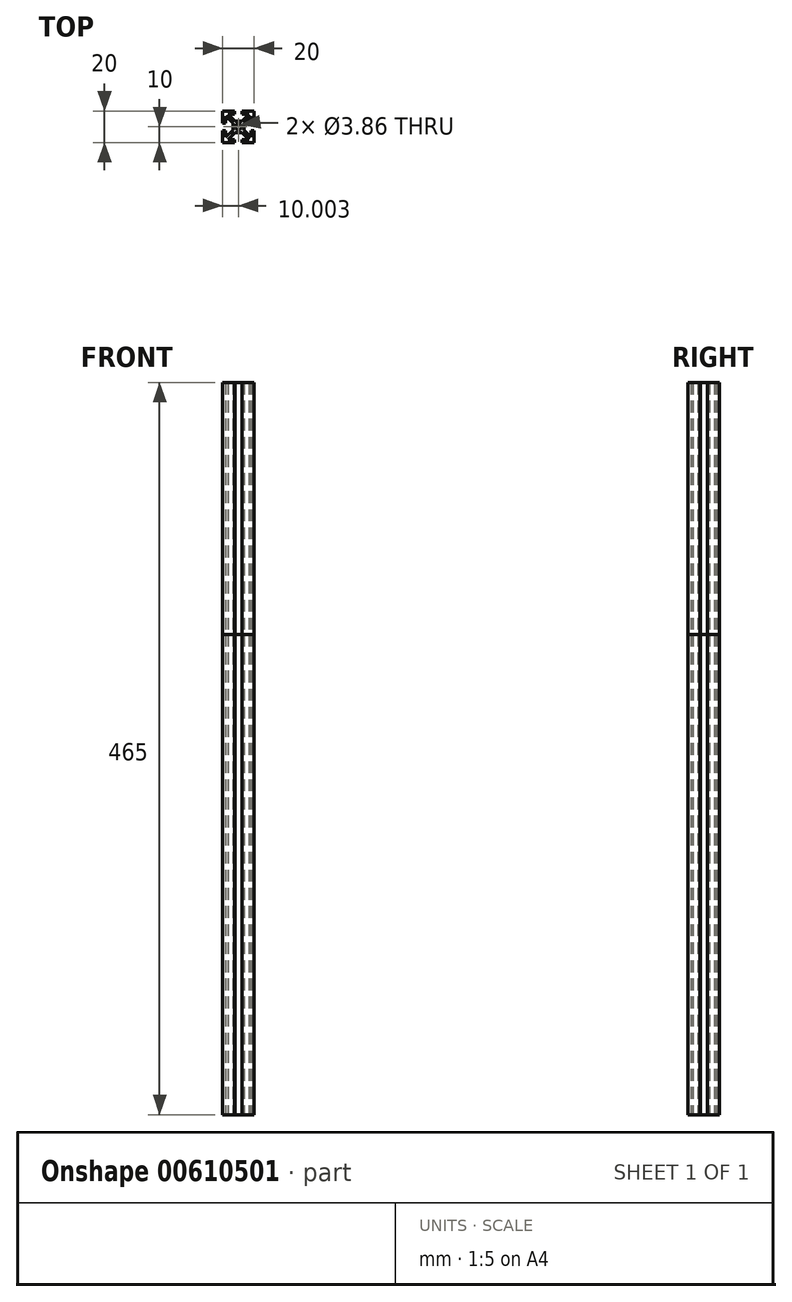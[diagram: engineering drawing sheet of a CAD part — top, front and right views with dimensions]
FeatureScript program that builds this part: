
annotation { "Feature Type Name" : "Feature", "Feature Type Description" : "" }
export const myFeature = defineFeature(function(context is Context, id is Id, definition is map)
    precondition{}
    {
        {
            var Q0;
            Q0=qCreatedBy(makeId("Top.planeOp"),FACE);
            var sketch = newSketch(context, id + "F0", { "sketchPlane" : qUnion([Q0])});
            skCircle(sketch, "E0.0", {"center": v(0, 0) * mm, "radius": 1.93 * mm});
            skLineSegment(sketch, "E0.1", {"start": v(-2.2, 3.6) * mm, "end": v(2.2, 3.6) * mm});
            skLineSegment(sketch, "E0.2", {"start": v(-6.72, 8.13) * mm, "end": v(-2.2, 3.6) * mm});
            skLineSegment(sketch, "E0.3", {"start": v(-3.6, 2.24) * mm, "end": v(-8.1, 6.74) * mm});
            skLineSegment(sketch, "E0.4", {"start": v(-8.1, 6.74) * mm, "end": v(-8.1, 2.38) * mm});
            skLineSegment(sketch, "E0.5", {"start": v(-8.1, 2.38) * mm, "end": v(-10, 2.38) * mm});
            skLineSegment(sketch, "E0.6", {"start": v(-10, 2.38) * mm, "end": v(-10, 10) * mm});
            skLineSegment(sketch, "E0.7", {"start": v(-10, 10) * mm, "end": v(-2.38, 10) * mm});
            skLineSegment(sketch, "E0.8", {"start": v(-2.38, 10) * mm, "end": v(-2.38, 8.13) * mm});
            skLineSegment(sketch, "E0.9", {"start": v(-2.38, 8.13) * mm, "end": v(-6.72, 8.13) * mm});
            skLineSegment(sketch, "E0.10", {"start": v(2.2, 3.6) * mm, "end": v(6.73, 8.13) * mm});
            skLineSegment(sketch, "E0.11", {"start": v(8.1, 6.74) * mm, "end": v(3.6, 2.24) * mm});
            skLineSegment(sketch, "E0.12", {"start": v(2.38, 8.13) * mm, "end": v(6.73, 8.13) * mm});
            skLineSegment(sketch, "E0.13", {"start": v(2.38, 8.13) * mm, "end": v(2.38, 10) * mm});
            skLineSegment(sketch, "E0.14", {"start": v(2.38, 10) * mm, "end": v(10, 10) * mm});
            skLineSegment(sketch, "E0.15", {"start": v(10, 10) * mm, "end": v(10, 2.38) * mm});
            skLineSegment(sketch, "E0.16", {"start": v(8.1, 2.38) * mm, "end": v(8.1, 6.74) * mm});
            skLineSegment(sketch, "E0.17", {"start": v(10, 2.38) * mm, "end": v(8.1, 2.38) * mm});
            skLineSegment(sketch, "E0.18", {"start": v(3.6, 2.24) * mm, "end": v(3.6, -2.24) * mm});
            skLineSegment(sketch, "E0.19", {"start": v(3.6, -2.24) * mm, "end": v(8.1, -6.74) * mm});
            skLineSegment(sketch, "E0.20", {"start": v(8.1, -6.74) * mm, "end": v(8.1, -2.38) * mm});
            skLineSegment(sketch, "E0.21", {"start": v(8.1, -2.38) * mm, "end": v(10, -2.38) * mm});
            skLineSegment(sketch, "E0.22", {"start": v(10, -2.38) * mm, "end": v(10, -10) * mm});
            skLineSegment(sketch, "E0.23", {"start": v(10, -10) * mm, "end": v(2.38, -10) * mm});
            skLineSegment(sketch, "E0.24", {"start": v(2.38, -10) * mm, "end": v(2.38, -8.13) * mm});
            skLineSegment(sketch, "E0.25", {"start": v(2.38, -8.13) * mm, "end": v(6.72, -8.13) * mm});
            skLineSegment(sketch, "E0.26", {"start": v(6.72, -8.13) * mm, "end": v(2.2, -3.6) * mm});
            skLineSegment(sketch, "E0.27", {"start": v(2.2, -3.6) * mm, "end": v(-2.2, -3.6) * mm});
            skLineSegment(sketch, "E0.28", {"start": v(-2.2, -3.6) * mm, "end": v(-6.73, -8.13) * mm});
            skLineSegment(sketch, "E0.29", {"start": v(-8.1, -6.74) * mm, "end": v(-3.6, -2.24) * mm});
            skLineSegment(sketch, "E0.30", {"start": v(-3.6, -2.24) * mm, "end": v(-3.6, 2.24) * mm});
            skLineSegment(sketch, "E0.31", {"start": v(-8.1, -2.38) * mm, "end": v(-8.1, -6.74) * mm});
            skLineSegment(sketch, "E0.32", {"start": v(-10, -2.38) * mm, "end": v(-8.1, -2.38) * mm});
            skLineSegment(sketch, "E0.33", {"start": v(-10, -10) * mm, "end": v(-10, -2.38) * mm});
            skLineSegment(sketch, "E0.34", {"start": v(-2.38, -10) * mm, "end": v(-10, -10) * mm});
            skLineSegment(sketch, "E0.35", {"start": v(-6.73, -8.13) * mm, "end": v(-2.38, -8.13) * mm});
            skLineSegment(sketch, "E0.36", {"start": v(-2.38, -8.13) * mm, "end": v(-2.38, -10) * mm});
            skSolve(sketch);
        }
        {
            var Q0;
            Q0=makeQuery(id+"F0.imprint","IMPRINT",FACE,{"disambiguationData":[TD([[makeQuery(id+"F0.imprint","IMPRINT",EDGE,{"derivedFrom":sQuery(id+"F0.wireOp",EDGE,"E0.0")}),-1.0]])]});
            extrude(context, id + "F1", {"entities" : qUnion([Q0]), "depth" : 305 * mm, "offsetDistance" : 25.4 * mm});
        }
        {
            var Q0;
            Q0=makeQuery(id+"F1.opExtrude","CAP_FACE",FACE,{"disambiguationData":[OSD([sQuery(id+"F0.wireOp",EDGE,"E0.0"),sQuery(id+"F0.wireOp",EDGE,"E0.1"),sQuery(id+"F0.wireOp",EDGE,"E0.2"),sQuery(id+"F0.wireOp",EDGE,"E0.3"),sQuery(id+"F0.wireOp",EDGE,"E0.4"),sQuery(id+"F0.wireOp",EDGE,"E0.5"),sQuery(id+"F0.wireOp",EDGE,"E0.6"),sQuery(id+"F0.wireOp",EDGE,"E0.7"),sQuery(id+"F0.wireOp",EDGE,"E0.8"),sQuery(id+"F0.wireOp",EDGE,"E0.9"),sQuery(id+"F0.wireOp",EDGE,"E0.10"),sQuery(id+"F0.wireOp",EDGE,"E0.11"),sQuery(id+"F0.wireOp",EDGE,"E0.12"),sQuery(id+"F0.wireOp",EDGE,"E0.13"),sQuery(id+"F0.wireOp",EDGE,"E0.14"),sQuery(id+"F0.wireOp",EDGE,"E0.15"),sQuery(id+"F0.wireOp",EDGE,"E0.16"),sQuery(id+"F0.wireOp",EDGE,"E0.17"),sQuery(id+"F0.wireOp",EDGE,"E0.18"),sQuery(id+"F0.wireOp",EDGE,"E0.19"),sQuery(id+"F0.wireOp",EDGE,"E0.20"),sQuery(id+"F0.wireOp",EDGE,"E0.21"),sQuery(id+"F0.wireOp",EDGE,"E0.22"),sQuery(id+"F0.wireOp",EDGE,"E0.23"),sQuery(id+"F0.wireOp",EDGE,"E0.24"),sQuery(id+"F0.wireOp",EDGE,"E0.25"),sQuery(id+"F0.wireOp",EDGE,"E0.26"),sQuery(id+"F0.wireOp",EDGE,"E0.27"),sQuery(id+"F0.wireOp",EDGE,"E0.28"),sQuery(id+"F0.wireOp",EDGE,"E0.29"),sQuery(id+"F0.wireOp",EDGE,"E0.30"),sQuery(id+"F0.wireOp",EDGE,"E0.31"),sQuery(id+"F0.wireOp",EDGE,"E0.32"),sQuery(id+"F0.wireOp",EDGE,"E0.33"),sQuery(id+"F0.wireOp",EDGE,"E0.34"),sQuery(id+"F0.wireOp",EDGE,"E0.35"),sQuery(id+"F0.wireOp",EDGE,"E0.36")])],"isStart":false});
            extrude(context, id + "F2", {"entities" : qUnion([Q0]), "depth" : 160 * mm, "offsetDistance" : 25 * mm});
        }
    });
